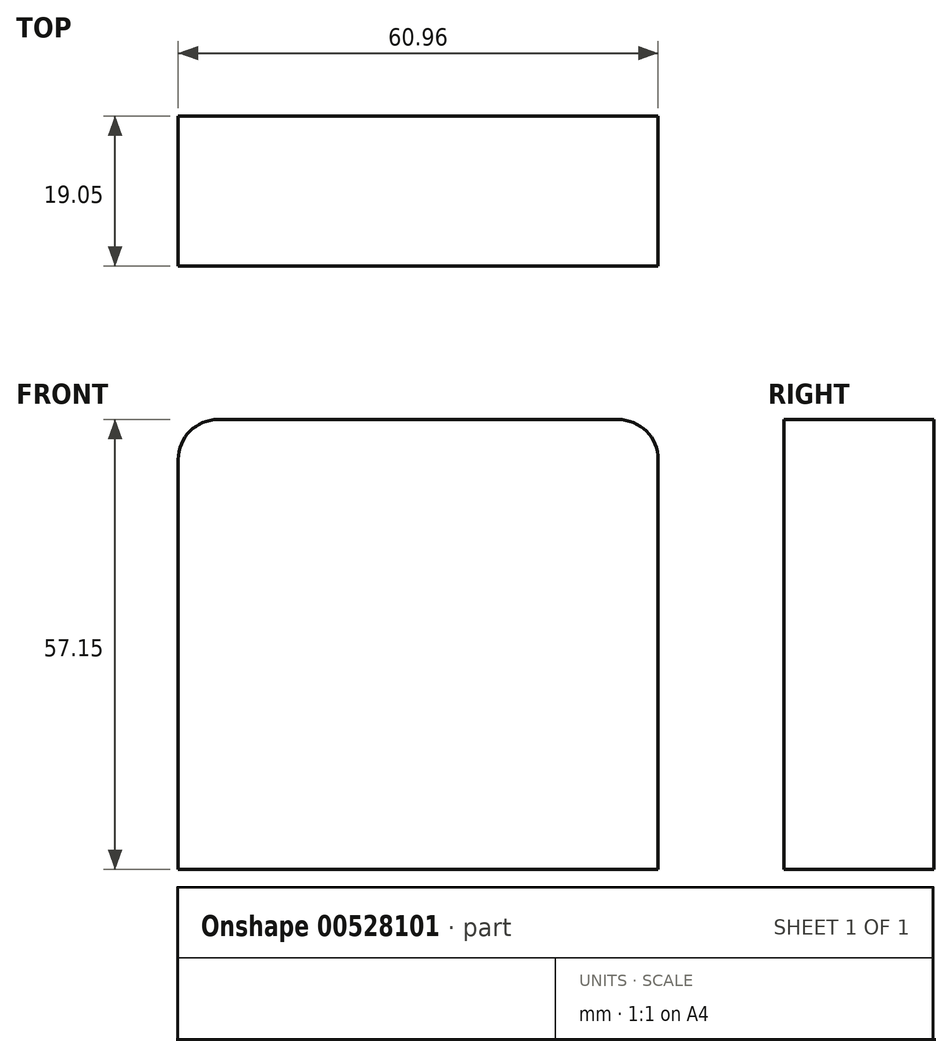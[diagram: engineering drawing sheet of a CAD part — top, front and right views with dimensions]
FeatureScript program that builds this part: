
annotation { "Feature Type Name" : "Feature", "Feature Type Description" : "" }
export const myFeature = defineFeature(function(context is Context, id is Id, definition is map)
    precondition{}
    {
        {
            var Q0;
            Q0=qCreatedBy(makeId("Top.planeOp"),FACE);
            var sketch = newSketch(context, id + "F0", { "sketchPlane" : qUnion([Q0])});
            skLineSegment(sketch, "E0.bottom", {"start": v(0, 0) * mm, "end": v(60.96, 0) * mm});
            skLineSegment(sketch, "E0.top", {"start": v(0, 19.05) * mm, "end": v(60.96, 19.05) * mm});
            skLineSegment(sketch, "E0.left", {"start": v(0, 0) * mm, "end": v(0, 19.05) * mm});
            skLineSegment(sketch, "E0.right", {"start": v(60.96, 0) * mm, "end": v(60.96, 19.05) * mm});
            skSolve(sketch);
        }
        {
            var Q0;
            Q0=makeQuery(id+"F0.imprint","IMPRINT",FACE,{"disambiguationData":[TD([[makeQuery(id+"F0.imprint","IMPRINT",EDGE,{"derivedFrom":sQuery(id+"F0.wireOp",EDGE,"E0.bottom")}),1.0]])]});
            extrude(context, id + "F1", {"entities" : qUnion([Q0]), "depth" : 57.15 * mm, "offsetDistance" : 25.4 * mm});
        }
        {
            var Q0;
            Q0=makeQuery(id+"F1.opExtrude","CAP_EDGE",EDGE,{"disambiguationData":[OSD([sQuery(id+"F0.wireOp",EDGE,"E0.right")])],"isStart":false});
            var Q1;
            Q1=makeQuery(id+"F1.opExtrude","CAP_EDGE",EDGE,{"disambiguationData":[OSD([sQuery(id+"F0.wireOp",EDGE,"E0.left")])],"isStart":false});
            fillet(context, id + "F2", {"entities" : qUnion([Q0, Q1]), "radius" : 5.08 * mm, "tangentPropagation" : true, "allowEdgeOverflow" : false});
        }
    });
